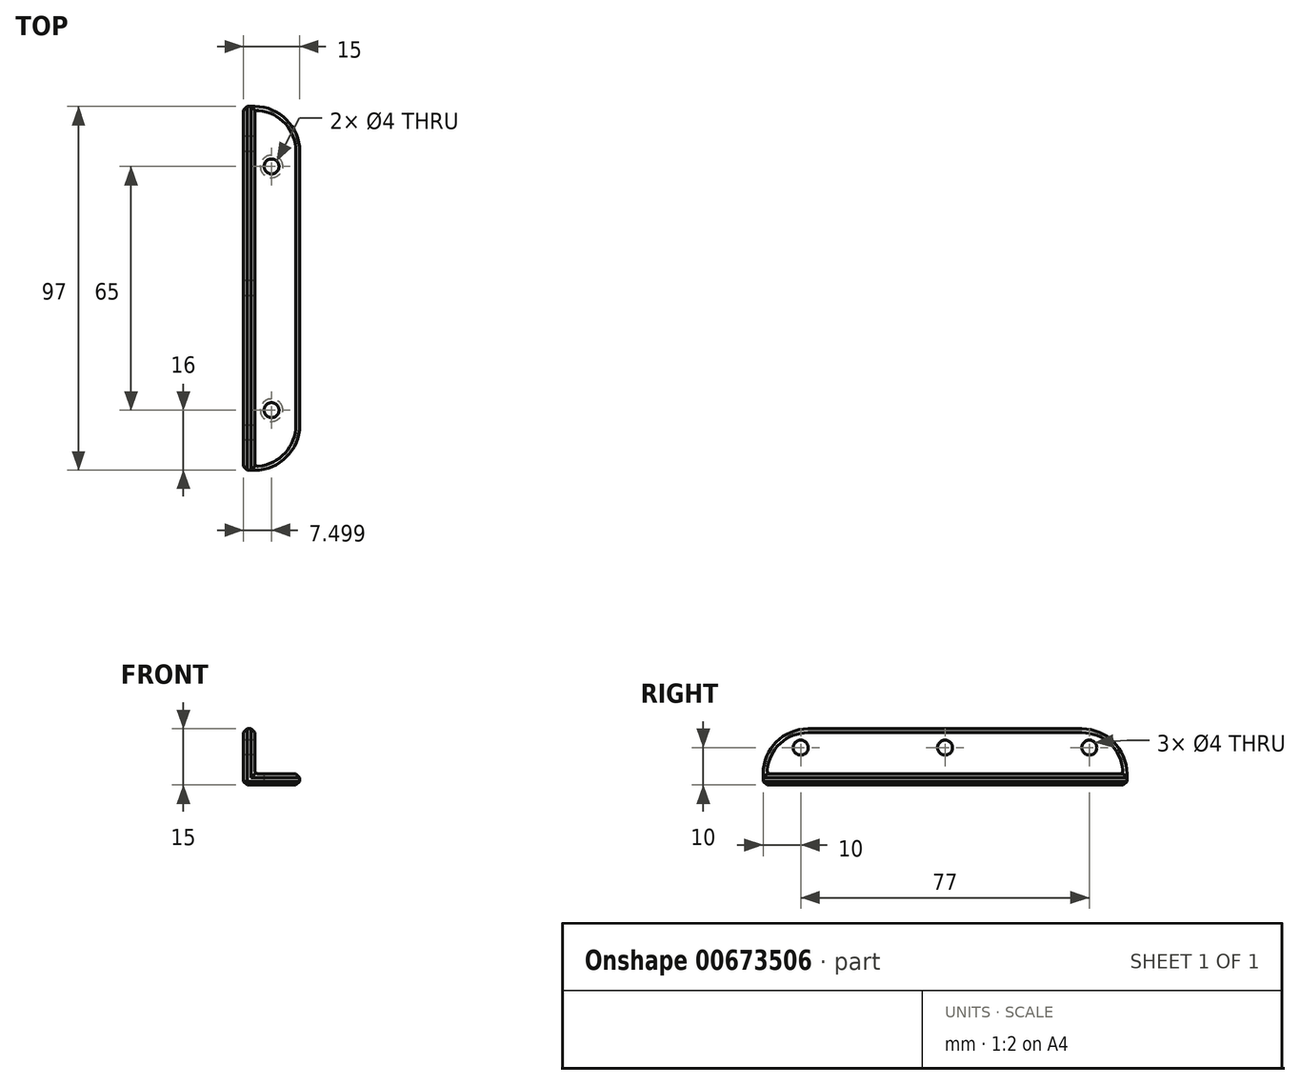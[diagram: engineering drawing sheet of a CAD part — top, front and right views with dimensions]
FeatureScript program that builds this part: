
annotation { "Feature Type Name" : "Feature", "Feature Type Description" : "" }
export const myFeature = defineFeature(function(context is Context, id is Id, definition is map)
    precondition{}
    {
        {
            var Q0;
            Q0=qCreatedBy(makeId("Front.planeOp"),FACE);
            var sketch = newSketch(context, id + "F0", { "sketchPlane" : qUnion([Q0])});
            skLineSegment(sketch, "E0", {"start": v(5.76, 15) * mm, "end": v(5.76, 0) * mm});
            skLineSegment(sketch, "E1", {"start": v(5.76, 0) * mm, "end": v(20.76, 0) * mm});
            skLineSegment(sketch, "E2", {"start": v(20.76, 0) * mm, "end": v(20.76, 3) * mm});
            skLineSegment(sketch, "E3", {"start": v(20.76, 3) * mm, "end": v(8.76, 3) * mm});
            skLineSegment(sketch, "E4", {"start": v(8.76, 3) * mm, "end": v(8.76, 15) * mm});
            skLineSegment(sketch, "E5", {"start": v(8.76, 15) * mm, "end": v(5.76, 15) * mm});
            skSolve(sketch);
        }
        {
            var Q0;
            Q0 = qSketchRegion(id + "F0", true);
            extrude(context, id + "F1", {"entities" : qUnion([Q0]), "depth" : 97 * mm, "offsetDistance" : 25 * mm});
        }
        {
            var Q0;
            Q0=makeQuery(id+"F1.opExtrude","SWEPT_FACE",FACE,{"disambiguationData":[OSD([sQuery(id+"F0.wireOp",EDGE,"E0")])]});
            var sketch = newSketch(context, id + "F2", { "sketchPlane" : qUnion([Q0])});
            skPoint(sketch, "E6.startSnap0", {"position": v(0, 7.5) * mm});
            skLineSegment(sketch, "E7", {"start": v(10, 10) * mm, "end": v(87, 10) * mm, "construction": true});
            skCircle(sketch, "E8", {"center": v(10, 10) * mm, "radius": 2 * mm});
            skCircle(sketch, "E9", {"center": v(87, 10) * mm, "radius": 2 * mm});
            skCircle(sketch, "E10", {"center": v(48.5, 10) * mm, "radius": 2 * mm});
            skSolve(sketch);
        }
        {
            var Q0;
            Q0 = qSketchRegion(id + "F2", true);
            extrude(context, id + "F3", {"entities" : qUnion([Q0]), "operationType" : NewBodyOperationType.REMOVE, "endBound" : BoundingType.THROUGH_ALL, "oppositeDirection" : true, "depth" : 25 * mm, "offsetDistance" : 25 * mm});
        }
        {
            var Q0;
            Q0=makeQuery(id+"F1.opExtrude","SWEPT_FACE",FACE,{"disambiguationData":[OSD([sQuery(id+"F0.wireOp",EDGE,"E1")])]});
            var sketch = newSketch(context, id + "F4", { "sketchPlane" : qUnion([Q0])});
            skLineSegment(sketch, "E11", {"start": v(13.26, 81) * mm, "end": v(13.26, 16) * mm, "construction": true});
            skCircle(sketch, "E12", {"center": v(13.26, 81) * mm, "radius": 2 * mm});
            skCircle(sketch, "E13", {"center": v(13.26, 16) * mm, "radius": 2 * mm});
            skLineSegment(sketch, "E14", {"start": v(13.26, 48.5) * mm, "end": v(5.76, 48.5) * mm, "construction": true});
            skPoint(sketch, "E15", {"position": v(5.76, 48.5) * mm});
            skSolve(sketch);
        }
        {
            var Q0;
            Q0 = qSketchRegion(id + "F4", true);
            extrude(context, id + "F5", {"entities" : qUnion([Q0]), "operationType" : NewBodyOperationType.REMOVE, "endBound" : BoundingType.THROUGH_ALL, "oppositeDirection" : true, "depth" : 25 * mm, "offsetDistance" : 25 * mm});
        }
        {
            var Q0;
            Q0=makeQuery(id+"F1.opExtrude","CAP_EDGE",EDGE,{"disambiguationData":[OSD([sQuery(id+"F0.wireOp",EDGE,"E5")])],"isStart":false});
            var Q1;
            Q1=makeQuery(id+"F1.opExtrude","CAP_EDGE",EDGE,{"disambiguationData":[OSD([sQuery(id+"F0.wireOp",EDGE,"E5")])],"isStart":true});
            var Q2;
            Q2=makeQuery(id+"F1.opExtrude","CAP_EDGE",EDGE,{"disambiguationData":[OSD([sQuery(id+"F0.wireOp",EDGE,"E2")])],"isStart":true});
            var Q3;
            Q3=makeQuery(id+"F1.opExtrude","CAP_EDGE",EDGE,{"disambiguationData":[OSD([sQuery(id+"F0.wireOp",EDGE,"E2")])],"isStart":false});
            fillet(context, id + "F6", {"entities" : qUnion([Q0, Q1, Q2, Q3]), "radius" : 12 * mm, "tangentPropagation" : true, "allowEdgeOverflow" : false});
        }
        {
            var Q0;
            Q0=makeQuery(id+"F1.opExtrude","SWEPT_EDGE",EDGE,{"disambiguationData":[OSD([sQuery(id+"F0.wireOp",EDGE,"E4"),sQuery(id+"F0.wireOp",EDGE,"E5")])]});
            var Q1;
            Q1=makeQuery(id+"F1.opExtrude","SWEPT_EDGE",EDGE,{"disambiguationData":[OSD([sQuery(id+"F0.wireOp",EDGE,"E2"),sQuery(id+"F0.wireOp",EDGE,"E3")])]});
            var Q2;
            Q2=makeQuery(id+"F1.opExtrude","SWEPT_FACE",FACE,{"disambiguationData":[OSD([sQuery(id+"F0.wireOp",EDGE,"E1")])]});
            var Q3;
            Q3=makeQuery(id+"F6.opFillet","BLEND_EDGE",EDGE,{"blendedFrom":[makeQuery(id+"F1.opExtrude","CAP_EDGE",EDGE,{"disambiguationData":[OSD([sQuery(id+"F0.wireOp",EDGE,"E5")])],"isStart":false}),makeQuery(id+"F1.opExtrude","SWEPT_FACE",FACE,{"disambiguationData":[OSD([sQuery(id+"F0.wireOp",EDGE,"E0")])]})],"blendedInto":[makeQuery(id+"F1.opExtrude","SWEPT_FACE",FACE,{"disambiguationData":[OSD([sQuery(id+"F0.wireOp",EDGE,"E0")])]})]});
            chamfer(context, id + "F7", {"entities" : qUnion([Q0, Q1, Q2, Q3]), "width" : 1 * mm, "tangentPropagation" : true});
        }
        {
            var Q0;
            Q0=makeQuery(id+"F1.opExtrude","SWEPT_EDGE",EDGE,{"disambiguationData":[OSD([sQuery(id+"F0.wireOp",EDGE,"E3"),sQuery(id+"F0.wireOp",EDGE,"E4")])]});
            fillet(context, id + "F8", {"entities" : qUnion([Q0]), "radius" : 1 * mm, "tangentPropagation" : true, "allowEdgeOverflow" : false});
        }
    });
